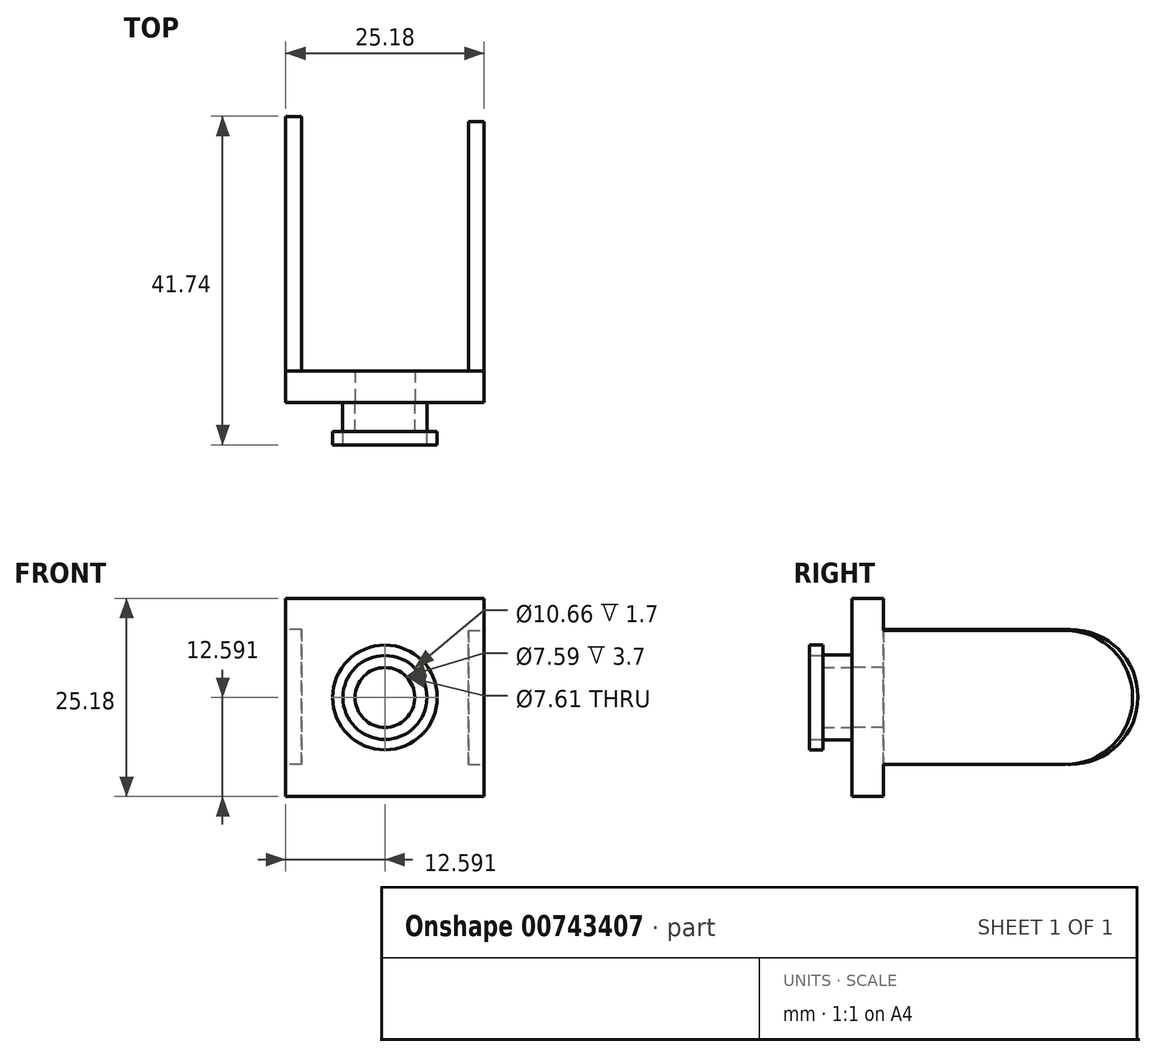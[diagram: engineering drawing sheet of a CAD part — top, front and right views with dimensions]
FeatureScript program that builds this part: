
annotation { "Feature Type Name" : "Feature", "Feature Type Description" : "" }
export const myFeature = defineFeature(function(context is Context, id is Id, definition is map)
    precondition{}
    {
        {
            var Q0;
            Q0=qCreatedBy(makeId("Front.planeOp"),FACE);
            var sketch = newSketch(context, id + "F0", { "sketchPlane" : qUnion([Q0])});
            skLineSegment(sketch, "E0", {"start": v(0, 0) * mm, "end": v(0, 25.18) * mm});
            skLineSegment(sketch, "E1", {"start": v(0, 25.18) * mm, "end": v(25.18, 25.18) * mm});
            skLineSegment(sketch, "E2", {"start": v(25.18, 25.18) * mm, "end": v(25.18, 0) * mm});
            skLineSegment(sketch, "E3", {"start": v(25.18, 0) * mm, "end": v(0, 0) * mm});
            skSolve(sketch);
        }
        {
            var Q0;
            Q0 = qSketchRegion(id + "F0", true);
            extrude(context, id + "F1", {"entities" : qUnion([Q0]), "depth" : 4 * mm, "offsetDistance" : 25 * mm});
        }
        {
            var Q0;
            Q0=makeQuery(id+"F1.opExtrude","CAP_FACE",FACE,{"disambiguationData":[OSD([sQuery(id+"F0.wireOp",EDGE,"E0"),sQuery(id+"F0.wireOp",EDGE,"E1"),sQuery(id+"F0.wireOp",EDGE,"E2"),sQuery(id+"F0.wireOp",EDGE,"E3")])],"isStart":false});
            var sketch = newSketch(context, id + "F2", { "sketchPlane" : qUnion([Q0])});
            skCircle(sketch, "E4", {"center": v(12.6, 12.6) * mm, "radius": 3.8 * mm});
            skPoint(sketch, "E4.centerSnap0", {"position": v(12.6, 25.18) * mm});
            skPoint(sketch, "E4.centerSnap1", {"position": v(0, 12.6) * mm});
            skCircle(sketch, "E5", {"center": v(12.6, 12.6) * mm, "radius": 5.38 * mm});
            skSolve(sketch);
        }
        {
            var Q0;
            Q0 = qSketchRegion(id + "F2", true);
            extrude(context, id + "F3", {"entities" : qUnion([Q0]), "operationType" : NewBodyOperationType.ADD, "depth" : 3.7 * mm, "offsetDistance" : 25 * mm});
        }
        {
            var Q0;
            Q0=makeQuery(id+"F3.opExtrude","CAP_FACE",FACE,{"disambiguationData":[OSD([sQuery(id+"F2.wireOp",EDGE,"E4"),sQuery(id+"F2.wireOp",EDGE,"E5")])],"isStart":false});
            var sketch = newSketch(context, id + "F4", { "sketchPlane" : qUnion([Q0])});
            skCircle(sketch, "E6", {"center": v(12.6, 12.6) * mm, "radius": 5.33 * mm});
            skCircle(sketch, "E7", {"center": v(12.6, 12.6) * mm, "radius": 6.65 * mm});
            skSolve(sketch);
        }
        {
            var Q0;
            Q0 = qSketchRegion(id + "F4", true);
            extrude(context, id + "F5", {"entities" : qUnion([Q0]), "operationType" : NewBodyOperationType.ADD, "depth" : 1.7 * mm, "offsetDistance" : 25 * mm});
        }
        {
            var Q0;
            Q0=makeQuery(id+"F3.boolean.opBoolean","SPLIT",FACE,{"disambiguationData":[TD([makeQuery(id+"F3.opExtrude","SWEPT_FACE",FACE,{"disambiguationData":[OSD([sQuery(id+"F2.wireOp",EDGE,"E4")])]})])],"derivedFrom":makeQuery(id+"F1.opExtrude","CAP_FACE",FACE,{"disambiguationData":[OSD([sQuery(id+"F0.wireOp",EDGE,"E0"),sQuery(id+"F0.wireOp",EDGE,"E1"),sQuery(id+"F0.wireOp",EDGE,"E2"),sQuery(id+"F0.wireOp",EDGE,"E3")])],"isStart":false})});
            var sketch = newSketch(context, id + "F6", { "sketchPlane" : qUnion([Q0])});
            skCircle(sketch, "E8", {"center": v(12.6, 12.6) * mm, "radius": 3.8 * mm});
            skSolve(sketch);
        }
        {
            var Q0;
            Q0 = qSketchRegion(id + "F6", true);
            extrude(context, id + "F7", {"entities" : qUnion([Q0]), "operationType" : NewBodyOperationType.REMOVE, "oppositeDirection" : true, "depth" : 25 * mm, "offsetDistance" : 25 * mm});
        }
        {
            var Q0;
            Q0=makeQuery(id+"F1.opExtrude","SWEPT_FACE",FACE,{"disambiguationData":[OSD([sQuery(id+"F0.wireOp",EDGE,"E2")])]});
            var sketch = newSketch(context, id + "F8", { "sketchPlane" : qUnion([Q0])});
            skLineSegment(sketch, "E9", {"start": v(0, 25.18) * mm, "end": v(0, 21.1) * mm});
            skLineSegment(sketch, "E10", {"start": v(0, 0) * mm, "end": v(0, 4.08) * mm});
            skLineSegment(sketch, "E11", {"start": v(0, 4.08) * mm, "end": v(23.15, 4.08) * mm});
            skLineSegment(sketch, "E12", {"start": v(0, 21.1) * mm, "end": v(23.15, 21.1) * mm});
            skArc(sketch, "E13", {"start": v(23.15, 4.08) * mm, "mid": v(31.66, 12.6) * mm, "end": v(23.15, 21.1) * mm});
            skSolve(sketch);
        }
        {
            var Q0;
            Q0 = qSketchRegion(id + "F8", true);
            var Q1;
            {var subQ0=sQuery(id+"F8.wireOp",EDGE,"E11");Q1=makeQuery(id+"F8.imprint","IMPRINT",FACE,{"disambiguationData":[TD([[makeQuery(id+"F8.imprint","IMPRINT",EDGE,{"derivedFrom":subQ0}),1.0]])]});}
            extrude(context, id + "F9", {"entities" : qUnion([Q0, Q1]), "operationType" : NewBodyOperationType.ADD, "oppositeDirection" : true, "depth" : 2 * mm, "offsetDistance" : 25 * mm});
        }
        {
            var Q0;
            Q0=makeQuery(id+"F1.opExtrude","SWEPT_FACE",FACE,{"disambiguationData":[OSD([sQuery(id+"F0.wireOp",EDGE,"E0")])]});
            var sketch = newSketch(context, id + "F10", { "sketchPlane" : qUnion([Q0])});
            skLineSegment(sketch, "E14", {"start": v(0, 25.18) * mm, "end": v(0, 21.24) * mm});
            skLineSegment(sketch, "E15", {"start": v(0, 0) * mm, "end": v(0, 4.09) * mm});
            skLineSegment(sketch, "E16", {"start": v(0, 4.09) * mm, "end": v(-23.76, 4.09) * mm});
            skLineSegment(sketch, "E17", {"start": v(0, 21.24) * mm, "end": v(-23.76, 21.24) * mm});
            skArc(sketch, "E18", {"start": v(-23.76, 21.24) * mm, "mid": v(-32.34, 12.66) * mm, "end": v(-23.76, 4.09) * mm});
            skSolve(sketch);
        }
        {
            var Q0;
            Q0 = qSketchRegion(id + "F10", true);
            var Q1;
            {var subQ0=sQuery(id+"F10.wireOp",EDGE,"E16");Q1=makeQuery(id+"F10.imprint","IMPRINT",FACE,{"disambiguationData":[TD([[makeQuery(id+"F10.imprint","IMPRINT",EDGE,{"derivedFrom":subQ0}),-1.0]])]});}
            extrude(context, id + "F11", {"entities" : qUnion([Q0, Q1]), "operationType" : NewBodyOperationType.ADD, "oppositeDirection" : true, "depth" : 2 * mm, "offsetDistance" : 25 * mm});
        }
    });
